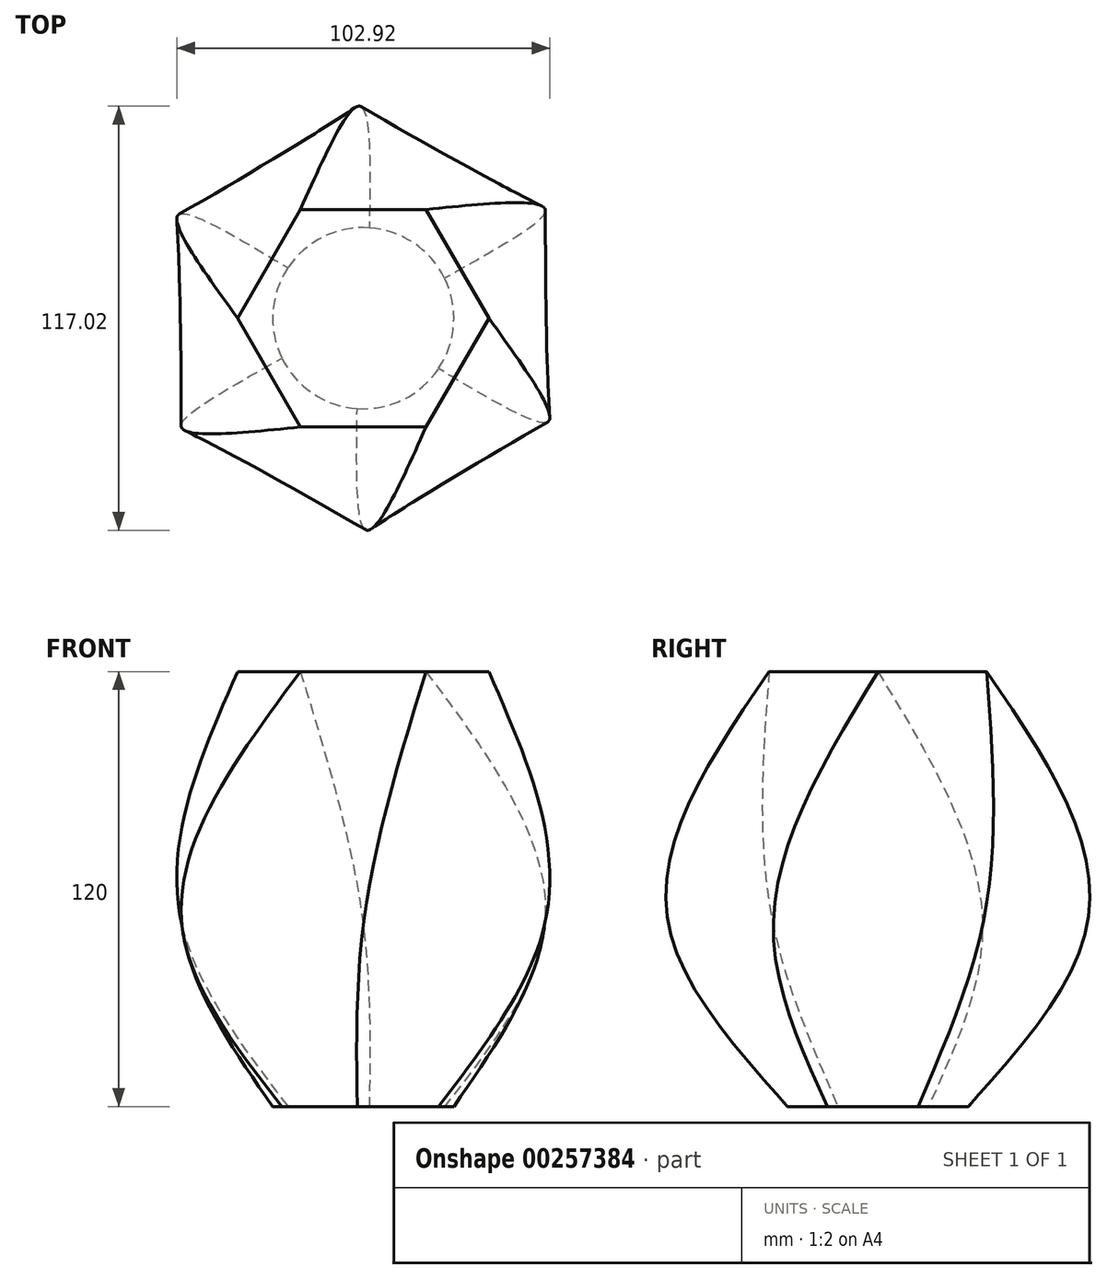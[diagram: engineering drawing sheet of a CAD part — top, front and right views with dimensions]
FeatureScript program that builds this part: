
annotation { "Feature Type Name" : "Feature", "Feature Type Description" : "" }
export const myFeature = defineFeature(function(context is Context, id is Id, definition is map)
    precondition{}
    {
        {
            var Q0;
            Q0=qCreatedBy(makeId("Top.planeOp"),FACE);
            var sketch = newSketch(context, id + "F0", { "sketchPlane" : qUnion([Q0])});
            skCircle(sketch, "E0.cCircle", {"center": v(0, 0) * mm, "radius": 50 * mm, "construction": true});
            skLineSegment(sketch, "E0.0", {"start": v(50, 28.87) * mm, "end": v(50, -28.87) * mm});
            skLineSegment(sketch, "E0.1", {"start": v(50, -28.87) * mm, "end": v(0, -57.74) * mm});
            skLineSegment(sketch, "E0.2", {"start": v(0, -57.74) * mm, "end": v(-50, -28.87) * mm});
            skLineSegment(sketch, "E0.3", {"start": v(-50, -28.87) * mm, "end": v(-50, 28.87) * mm});
            skLineSegment(sketch, "E0.4", {"start": v(-50, 28.87) * mm, "end": v(0, 57.74) * mm});
            skLineSegment(sketch, "E0.5", {"start": v(0, 57.74) * mm, "end": v(50, 28.87) * mm});
            skPoint(sketch, "E0.0.midPoint", {"position": v(50, 0) * mm});
            skSolve(sketch);
        }
        {
            var Q0;
            Q0=makeQuery(id+"F0.imprint","IMPRINT",FACE,{"disambiguationData":[TD([[makeQuery(id+"F0.imprint","IMPRINT",EDGE,{"derivedFrom":sQuery(id+"F0.wireOp",EDGE,"E0.0")}),-1.0]])]});
            cPlane(context, id + "F1", {"entities" : qUnion([Q0]), "cplaneType" : CPlaneType.OFFSET, "offset" : 70 * mm, "width" : 150 * mm, "height" : 150 * mm});
        }
        {
            var Q0;
            Q0=qCreatedBy(id+"F1.planeOp",FACE);
            var sketch = newSketch(context, id + "F2", { "sketchPlane" : qUnion([Q0])});
            skCircle(sketch, "E1.cCircle", {"center": v(0, 0) * mm, "radius": 30 * mm, "construction": true});
            skLineSegment(sketch, "E1.0", {"start": v(-17.32, 30) * mm, "end": v(17.32, 30) * mm});
            skLineSegment(sketch, "E1.1", {"start": v(17.32, 30) * mm, "end": v(34.64, 0) * mm});
            skLineSegment(sketch, "E1.2", {"start": v(34.64, 0) * mm, "end": v(17.32, -30) * mm});
            skLineSegment(sketch, "E1.3", {"start": v(17.32, -30) * mm, "end": v(-17.32, -30) * mm});
            skLineSegment(sketch, "E1.4", {"start": v(-17.32, -30) * mm, "end": v(-34.64, 0) * mm});
            skLineSegment(sketch, "E1.5", {"start": v(-34.64, 0) * mm, "end": v(-17.32, 30) * mm});
            skPoint(sketch, "E1.0.midPoint", {"position": v(0, 30) * mm});
            skSolve(sketch);
        }
        {
            var Q0;
            Q0=makeQuery(id+"F0.imprint","IMPRINT",FACE,{"disambiguationData":[TD([[makeQuery(id+"F0.imprint","IMPRINT",EDGE,{"derivedFrom":sQuery(id+"F0.wireOp",EDGE,"E0.0")}),-1.0]])]});
            cPlane(context, id + "F3", {"entities" : qUnion([Q0]), "cplaneType" : CPlaneType.OFFSET, "offset" : 50 * mm, "oppositeDirection" : true, "width" : 150 * mm, "height" : 150 * mm});
        }
        {
            var Q0;
            Q0=qCreatedBy(id+"F3.planeOp",FACE);
            var sketch = newSketch(context, id + "F4", { "sketchPlane" : qUnion([Q0])});
            skPoint(sketch, "E2.0", {"position": v(0, 0) * mm});
            skCircle(sketch, "E3", {"center": v(0, 0) * mm, "radius": 25 * mm});
            skPoint(sketch, "E4", {"position": v(-1.66, -24.94) * mm});
            skSolve(sketch);
        }
        {
            var Q0;
            Q0=makeQuery(id+"F2.imprint","IMPRINT",FACE,{"disambiguationData":[TD([[makeQuery(id+"F2.imprint","IMPRINT",EDGE,{"derivedFrom":sQuery(id+"F2.wireOp",EDGE,"E1.0")}),-1.0]])]});
            var Q1;
            Q1=makeQuery(id+"F0.imprint","IMPRINT",FACE,{"disambiguationData":[TD([[makeQuery(id+"F0.imprint","IMPRINT",EDGE,{"derivedFrom":sQuery(id+"F0.wireOp",EDGE,"E0.0")}),-1.0]])]});
            var Q2;
            Q2=makeQuery(id+"F4.imprint","IMPRINT",FACE,{"disambiguationData":[TD([[makeQuery(id+"F4.imprint","IMPRINT",EDGE,{"derivedFrom":sQuery(id+"F4.wireOp",EDGE,"E3")}),1.0]])]});
            var Q3;
            Q3=sQuery(id+"F0.wireOp",VERTEX,"E0.2.start");
            var Q4;
            Q4=sQuery(id+"F4.wireOp",VERTEX,"E4");
            var Q5;
            Q5=sQuery(id+"F2.wireOp",VERTEX,"E1.3.start");
            loft(context, id + "F5", {"sheetProfilesArray" : [{ "sheetProfileEntities" : qUnion([Q0]) }, { "sheetProfileEntities" : qUnion([Q1]) }, { "sheetProfileEntities" : qUnion([Q2]) }], "matchConnections" : true, "connections" : [{ "connectionEntities" : qUnion([Q3, Q4, Q5]), "connectionEdgeQueries" : qUnion([]), "connectionEdgeParameters" : [] }]});
        }
    });
